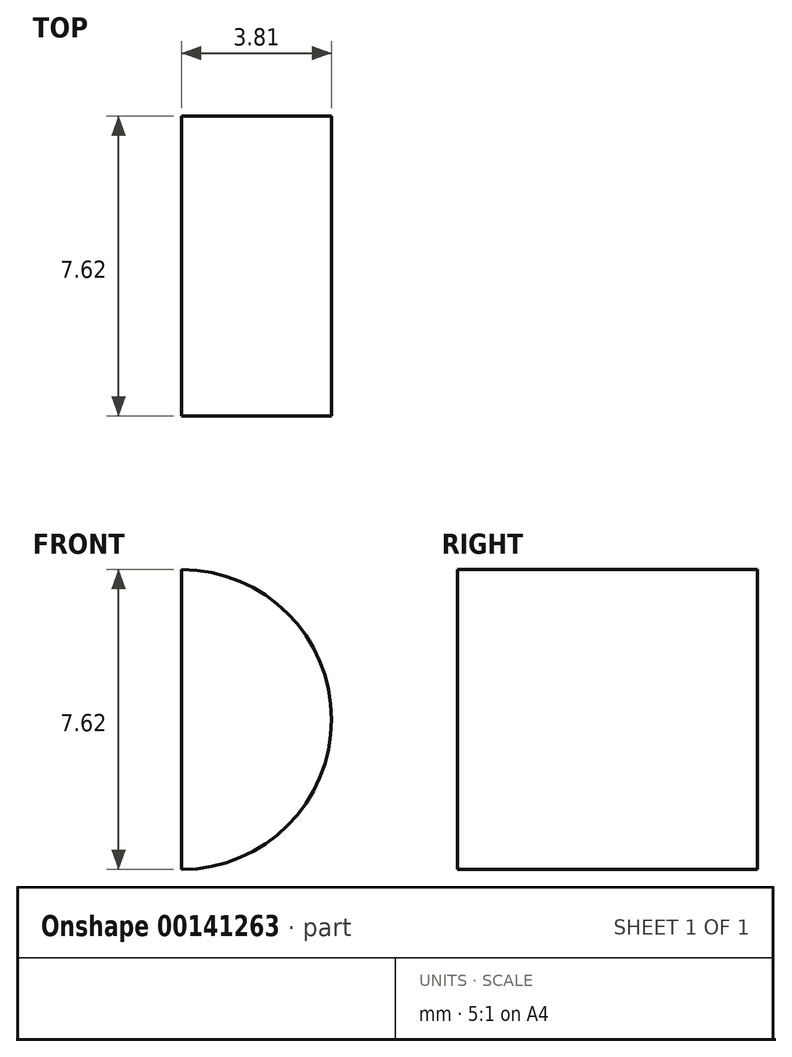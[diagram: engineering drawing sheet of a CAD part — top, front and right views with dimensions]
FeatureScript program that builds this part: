
annotation { "Feature Type Name" : "Feature", "Feature Type Description" : "" }
export const myFeature = defineFeature(function(context is Context, id is Id, definition is map)
    precondition{}
    {
        {
            var Q0;
            Q0=qCreatedBy(makeId("Front.planeOp"),FACE);
            var sketch = newSketch(context, id + "F0", { "sketchPlane" : qUnion([Q0])});
            skArc(sketch, "E0", {"start": v(0, -3.81) * mm, "mid": v(3.81, 0) * mm, "end": v(0, 3.81) * mm});
            skLineSegment(sketch, "E1", {"start": v(0, 3.81) * mm, "end": v(0, -3.81) * mm});
            skSolve(sketch);
        }
        {
            var Q0;
            Q0 = qSketchRegion(id + "F0", true);
            extrude(context, id + "F1", {"entities" : qUnion([Q0]), "depth" : 7.62 * mm});
        }
    });
